# Revit family: 9.Хомут SLK
name_source: partatom
category: Оборудование
revit_build: Autodesk Revit 2016 (Build: 20161004_0715(x64)
units: mm (PartAtom-declared; Revit-internal decimal feet)

## family parameters
Всегда вертикально = Да
На основе рабочей плоскости = Нет
Общий = Нет
При загрузке вырезать с полостями = Нет
Размер круглого соединителя = Использовать диаметр
Тип детали = Нормальный
Точка расчета площади = Нет

## types (6) — shared parameters
Единица измерения = шт.
Завод изготовитель = KORF
Ключевая пометка = Вентиляция
Материал = Сталь серая
Наименование и тех.хар-ка = Хомут
Раздел = ОВ
отступ = 20 мм

## per-type parameters (varying)
| type | x | А | Б | Д | Масса единицы | Тип, марка, обозначение | середина | х1 |
| 100 | 24 мм | 100 мм | 148 мм | 118 мм | 0.24 кг | SKL 100 | 15 мм | 28 мм |
| 160 | 36 мм | 160 мм | 212 мм | 178 мм | 0.32 кг | SKL 160 | 17 мм | 43 мм |
| 200 | 44 мм | 200 мм | 253 мм | 218 мм | 0.39 кг | SKL 200 | 18 мм | 52 мм |
| 250 | 54 мм | 250 мм | 304 мм | 268 мм | 0.46 кг | SKL 250 | 18 мм | 64 мм |
| 315 | 67 мм | 315 мм | 370 мм | 333 мм | 0.55 кг | SKL 315 | 19 мм | 80 мм |
| 125 | 29 мм | 125 мм | 174 мм | 145 мм | 0,27 кг | SKL 125 | 15 мм | 35 мм |
